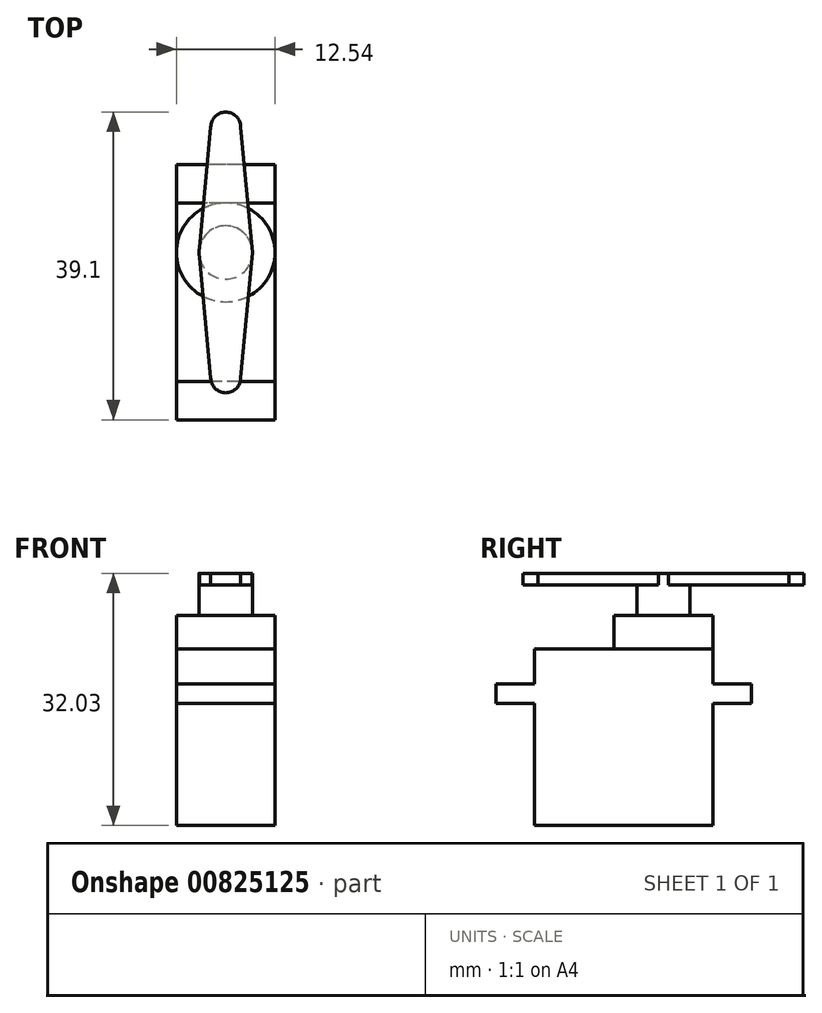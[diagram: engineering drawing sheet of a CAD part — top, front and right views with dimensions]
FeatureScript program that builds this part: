
annotation { "Feature Type Name" : "Feature", "Feature Type Description" : "" }
export const myFeature = defineFeature(function(context is Context, id is Id, definition is map)
    precondition{}
    {
        {
            var Q0;
            Q0=qCreatedBy(makeId("Top.planeOp"),FACE);
            var sketch = newSketch(context, id + "F0", { "sketchPlane" : qUnion([Q0])});
            skLineSegment(sketch, "E0.bottom", {"start": v(6.27, -11.33) * mm, "end": v(-6.27, -11.33) * mm});
            skLineSegment(sketch, "E0.top", {"start": v(6.27, 11.33) * mm, "end": v(-6.27, 11.33) * mm});
            skLineSegment(sketch, "E0.left", {"start": v(6.27, -11.33) * mm, "end": v(6.27, 11.33) * mm});
            skLineSegment(sketch, "E0.right", {"start": v(-6.27, -11.33) * mm, "end": v(-6.27, 11.33) * mm});
            skPoint(sketch, "E0.middle", {"position": v(0, 0) * mm});
            skSolve(sketch);
        }
        {
            var Q0;
            Q0 = qSketchRegion(id + "F0", true);
            extrude(context, id + "F1", {"entities" : qUnion([Q0]), "depth" : 22.43 * mm, "offsetDistance" : 25.4 * mm});
        }
        {
            var Q0;
            Q0=makeQuery(id+"F1.opExtrude","CAP_FACE",FACE,{"disambiguationData":[OSD([sQuery(id+"F0.wireOp",EDGE,"E0.bottom"),sQuery(id+"F0.wireOp",EDGE,"E0.top"),sQuery(id+"F0.wireOp",EDGE,"E0.left"),sQuery(id+"F0.wireOp",EDGE,"E0.right")])],"isStart":false});
            cPlane(context, id + "F2", {"entities" : qUnion([Q0]), "cplaneType" : CPlaneType.OFFSET, "offset" : 4.44 * mm, "oppositeDirection" : true, "width" : 152.4 * mm, "height" : 152.4 * mm});
        }
        {
            var Q0;
            Q0=qCreatedBy(id+"F2.planeOp",FACE);
            var sketch = newSketch(context, id + "F3", { "sketchPlane" : qUnion([Q0])});
            skLineSegment(sketch, "E1.0.0", {"start": v(6.27, -11.33) * mm, "end": v(6.27, 11.33) * mm});
            skLineSegment(sketch, "E1.0.1", {"start": v(6.27, 11.33) * mm, "end": v(-6.27, 11.33) * mm});
            skLineSegment(sketch, "E1.0.2", {"start": v(-6.27, 11.33) * mm, "end": v(-6.27, -11.33) * mm});
            skLineSegment(sketch, "E1.0.3", {"start": v(-6.27, -11.33) * mm, "end": v(6.27, -11.33) * mm});
            skLineSegment(sketch, "E2.bottom", {"start": v(6.27, 16.2) * mm, "end": v(-6.27, 16.2) * mm});
            skLineSegment(sketch, "E2.top", {"start": v(6.27, -16.2) * mm, "end": v(-6.27, -16.2) * mm});
            skLineSegment(sketch, "E2.left", {"start": v(6.27, 16.2) * mm, "end": v(6.27, -16.2) * mm});
            skLineSegment(sketch, "E2.right", {"start": v(-6.27, 16.2) * mm, "end": v(-6.27, -16.2) * mm});
            skSolve(sketch);
        }
        {
            var Q0;
            Q0 = qSketchRegion(id + "F3", true);
            extrude(context, id + "F4", {"entities" : qUnion([Q0]), "operationType" : NewBodyOperationType.ADD, "oppositeDirection" : true, "depth" : 2.48 * mm, "offsetDistance" : 25.4 * mm});
        }
        {
            var Q0;
            Q0=makeQuery(id+"F1.opExtrude","CAP_FACE",FACE,{"disambiguationData":[OSD([sQuery(id+"F0.wireOp",EDGE,"E0.bottom"),sQuery(id+"F0.wireOp",EDGE,"E0.top"),sQuery(id+"F0.wireOp",EDGE,"E0.left"),sQuery(id+"F0.wireOp",EDGE,"E0.right")])],"isStart":false});
            var sketch = newSketch(context, id + "F5", { "sketchPlane" : qUnion([Q0])});
            skLineSegment(sketch, "E3.0.0", {"start": v(6.27, -11.33) * mm, "end": v(6.27, 11.33) * mm});
            skLineSegment(sketch, "E3.0.1", {"start": v(6.27, 11.33) * mm, "end": v(-6.27, 11.33) * mm});
            skLineSegment(sketch, "E3.0.2", {"start": v(-6.27, 11.33) * mm, "end": v(-6.27, -11.33) * mm});
            skLineSegment(sketch, "E3.0.3", {"start": v(-6.27, -11.33) * mm, "end": v(6.27, -11.33) * mm});
            skCircle(sketch, "E4", {"center": v(0, 5.05) * mm, "radius": 6.27 * mm});
            skSolve(sketch);
        }
        {
            var Q0;
            {var subQ0=sQuery(id+"F5.wireOp",EDGE,"E4");var subQ1=makeQuery(id+"F5.imprint","INTERSECT",VERTEX,{"derivedFrom":[sQuery(id+"F5.wireOp",EDGE,"E3.0.0"),subQ0]});Q0=makeQuery(id+"F5.imprint","IMPRINT",FACE,{"disambiguationData":[TD([[makeQuery(id+"F5.imprint","IMPRINT",EDGE,{"disambiguationData":[TD([[subQ1,-1.0]])],"derivedFrom":subQ0}),1.0]])]});}
            extrude(context, id + "F6", {"entities" : qUnion([Q0]), "operationType" : NewBodyOperationType.ADD, "depth" : 4.27 * mm, "offsetDistance" : 25.4 * mm});
        }
        {
            var Q0;
            Q0=makeQuery(id+"F6.opExtrude","CAP_FACE",FACE,{"disambiguationData":[OSD([sQuery(id+"F5.wireOp",EDGE,"E4")])],"isStart":false});
            var sketch = newSketch(context, id + "F7", { "sketchPlane" : qUnion([Q0])});
            skCircle(sketch, "E5", {"center": v(0, 5.05) * mm, "radius": 3.4 * mm});
            skSolve(sketch);
        }
        {
            var Q0;
            Q0 = qSketchRegion(id + "F7", true);
            extrude(context, id + "F8", {"entities" : qUnion([Q0]), "operationType" : NewBodyOperationType.ADD, "depth" : 5.33 * mm, "offsetDistance" : 25.4 * mm});
        }
        {
            var Q0;
            Q0=makeQuery(id+"F8.opExtrude","CAP_FACE",FACE,{"disambiguationData":[OSD([sQuery(id+"F7.wireOp",EDGE,"E5")])],"isStart":false});
            var sketch = newSketch(context, id + "F9", { "sketchPlane" : qUnion([Q0])});
            skArc(sketch, "E6.0", {"start": v(3.33, 4.43) * mm, "mid": v(3.4, 5.05) * mm, "end": v(3.33, 5.68) * mm});
            skArc(sketch, "E7", {"start": v(1.9, 20.98) * mm, "mid": v(0, 22.89) * mm, "end": v(-1.9, 20.98) * mm});
            skArc(sketch, "E8", {"start": v(-1.9, -10.87) * mm, "mid": v(0, -12.78) * mm, "end": v(1.9, -10.87) * mm});
            skLineSegment(sketch, "E9", {"start": v(1.9, 20.98) * mm, "end": v(3.4, 5.05) * mm});
            skLineSegment(sketch, "E10", {"start": v(1.9, -10.87) * mm, "end": v(3.4, 5.05) * mm});
            skPoint(sketch, "E11.orphan", {"position": v(-2.5, 20.98) * mm});
            skLineSegment(sketch, "E12", {"start": v(-1.9, 20.98) * mm, "end": v(-3.4, 5.05) * mm});
            skLineSegment(sketch, "E13", {"start": v(-3.4, 5.05) * mm, "end": v(-1.9, -10.87) * mm});
            skArc(sketch, "E14.trimOffspring", {"start": v(-3.33, 5.68) * mm, "mid": v(-3.4, 5.05) * mm, "end": v(-3.33, 4.43) * mm});
            skSolve(sketch);
        }
        {
            var Q0;
            Q0 = qSketchRegion(id + "F9", true);
            extrude(context, id + "F10", {"entities" : qUnion([Q0]), "operationType" : NewBodyOperationType.ADD, "oppositeDirection" : true, "depth" : 1.47 * mm, "offsetDistance" : 25.4 * mm});
        }
    });
